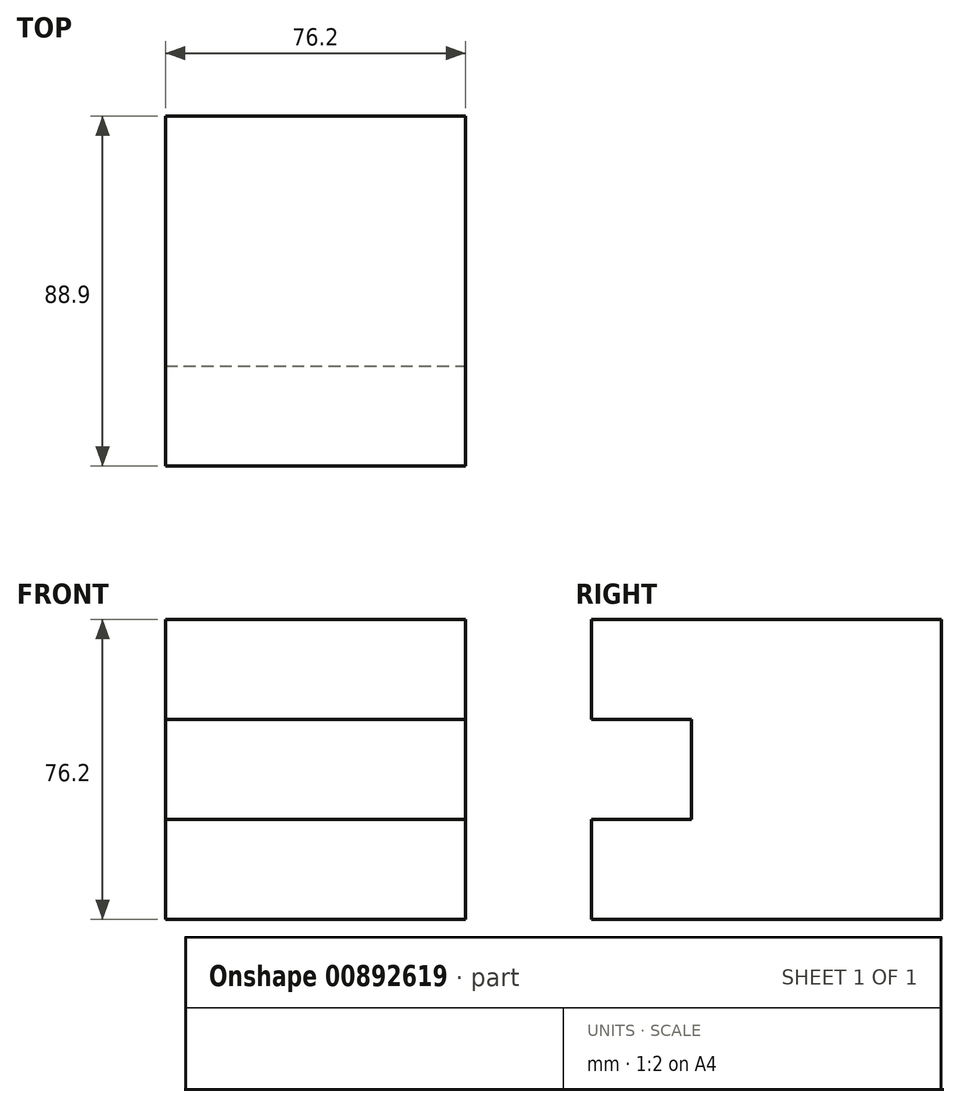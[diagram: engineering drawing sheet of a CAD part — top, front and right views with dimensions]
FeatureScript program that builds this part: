
annotation { "Feature Type Name" : "Feature", "Feature Type Description" : "" }
export const myFeature = defineFeature(function(context is Context, id is Id, definition is map)
    precondition{}
    {
        {
            var Q0;
            Q0=qCreatedBy(makeId("Top.planeOp"),FACE);
            var sketch = newSketch(context, id + "F0", { "sketchPlane" : qUnion([Q0])});
            skLineSegment(sketch, "E0.bottom", {"start": v(-34.95, 28.17) * mm, "end": v(41.25, 28.17) * mm});
            skLineSegment(sketch, "E0.top", {"start": v(-34.95, -35.33) * mm, "end": v(41.25, -35.33) * mm});
            skLineSegment(sketch, "E0.left", {"start": v(-34.95, 28.17) * mm, "end": v(-34.95, -35.33) * mm});
            skLineSegment(sketch, "E0.right", {"start": v(41.25, 28.17) * mm, "end": v(41.25, -35.33) * mm});
            skSolve(sketch);
        }
        {
            var Q0;
            Q0 = qSketchRegion(id + "F0", true);
            extrude(context, id + "F1", {"entities" : qUnion([Q0]), "depth" : 76.2 * mm, "offsetDistance" : 25.4 * mm});
        }
        {
            var Q0;
            Q0=makeQuery(id+"F1.opExtrude","SWEPT_FACE",FACE,{"disambiguationData":[OSD([sQuery(id+"F0.wireOp",EDGE,"E0.top")])]});
            var sketch = newSketch(context, id + "F2", { "sketchPlane" : qUnion([Q0])});
            skLineSegment(sketch, "E1.bottom", {"start": v(-34.95, 76.2) * mm, "end": v(41.25, 76.2) * mm});
            skLineSegment(sketch, "E1.left", {"start": v(-34.95, 76.2) * mm, "end": v(-34.95, 50.8) * mm});
            skLineSegment(sketch, "E1.right", {"start": v(41.25, 76.2) * mm, "end": v(41.25, 50.8) * mm});
            skLineSegment(sketch, "E2", {"start": v(-34.95, 50.8) * mm, "end": v(41.25, 50.8) * mm});
            skLineSegment(sketch, "E3", {"start": v(-34.95, 0) * mm, "end": v(-34.95, 25.4) * mm});
            skLineSegment(sketch, "E4", {"start": v(-34.95, 25.4) * mm, "end": v(41.25, 25.4) * mm});
            skLineSegment(sketch, "E5", {"start": v(41.25, 25.4) * mm, "end": v(41.25, 0) * mm});
            skLineSegment(sketch, "E6", {"start": v(41.25, 0) * mm, "end": v(-34.95, 0) * mm});
            skSolve(sketch);
        }
        {
            var Q0;
            Q0 = qSketchRegion(id + "F2", true);
            extrude(context, id + "F3", {"entities" : qUnion([Q0]), "operationType" : NewBodyOperationType.ADD, "depth" : 25.4 * mm, "offsetDistance" : 25.4 * mm});
        }
    });
